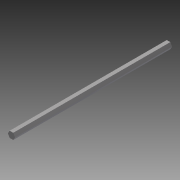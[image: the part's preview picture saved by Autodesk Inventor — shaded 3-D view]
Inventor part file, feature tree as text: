
AUTODESK INVENTOR PART (.ipt)
format: ipt  version: 2014 (Build 180170000, 170)  size: 76,800 bytes
history: native  units: in
note: dims shown in document units (in); Inventor stores cm internally (conversion verified against a paired STEP export)
features: extrude x1, sketch x1
ambient origin geometry x8: Origin, YZ Plane, XZ Plane, XY Plane, X Axis, Y Axis, Z Axis, Center Point
bodies: Solid1 (feature_tree)
feature tree (2):
  extrude  "Extrusion1"  Depth=9.5in TaperAngle=0.0deg
  sketch  "Sketch1"  dims[d0=0.375in d1=9.5in d2=0.0in]
